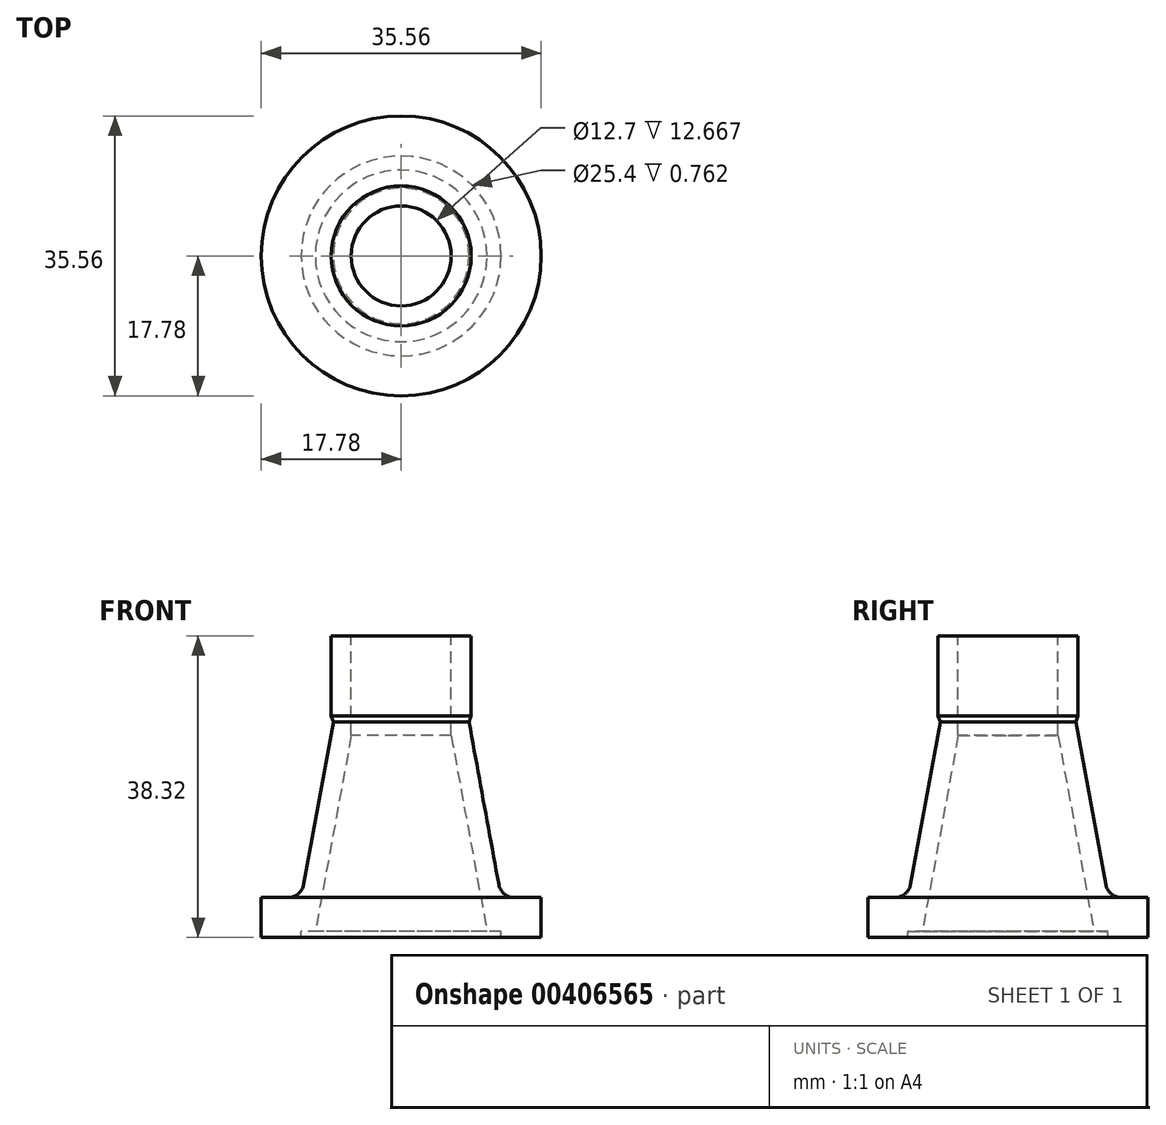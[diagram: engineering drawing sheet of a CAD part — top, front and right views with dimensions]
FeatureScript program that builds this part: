
annotation { "Feature Type Name" : "Feature", "Feature Type Description" : "" }
export const myFeature = defineFeature(function(context is Context, id is Id, definition is map)
    precondition{}
    {
        {
            var Q0;
            Q0=qCreatedBy(makeId("Front.planeOp"),FACE);
            var sketch = newSketch(context, id + "F0", { "sketchPlane" : qUnion([Q0])});
            skLineSegment(sketch, "E0", {"start": v(0, 25.5) * mm, "end": v(0, -29.47) * mm, "construction": true});
            skLineSegment(sketch, "E1", {"start": v(0, -17.71) * mm, "end": v(17.78, -17.71) * mm});
            skLineSegment(sketch, "E2", {"start": v(17.78, -17.71) * mm, "end": v(17.78, -12.63) * mm});
            skLineSegment(sketch, "E3", {"start": v(17.78, -12.63) * mm, "end": v(12.7, -12.63) * mm});
            skLineSegment(sketch, "E4", {"start": v(8.9, 10.45) * mm, "end": v(8.9, 20.61) * mm});
            skLineSegment(sketch, "E5", {"start": v(8.9, 20.61) * mm, "end": v(6.35, 20.61) * mm});
            skLineSegment(sketch, "E6", {"start": v(6.35, 20.61) * mm, "end": v(6.35, 7.94) * mm});
            skLineSegment(sketch, "E7", {"start": v(0, -16.95) * mm, "end": v(12.7, -16.95) * mm});
            skLineSegment(sketch, "E8", {"start": v(12.7, -16.95) * mm, "end": v(12.7, -17.71) * mm});
            skLineSegment(sketch, "E9", {"start": v(6.35, 20.61) * mm, "end": v(0, 20.61) * mm});
            skLineSegment(sketch, "E10", {"start": v(8.9, 10.45) * mm, "end": v(8.62, 9.67) * mm});
            skLineSegment(sketch, "E11", {"start": v(8.62, 9.67) * mm, "end": v(12.7, -12.63) * mm});
            skLineSegment(sketch, "E12", {"start": v(6.35, 7.94) * mm, "end": v(10.9, -16.95) * mm});
            skLineSegment(sketch, "E13", {"start": v(6.35, 7.94) * mm, "end": v(0, 7.94) * mm});
            skSolve(sketch);
        }
        {
            var Q0;
            {var subQ3=sQuery(id+"F0.wireOp",EDGE,"E2");Q0=makeQuery(id+"F0.imprint","IMPRINT",FACE,{"disambiguationData":[TD([[makeQuery(id+"F0.imprint","IMPRINT",EDGE,{"derivedFrom":subQ3}),1.0]])]});}
            var Q1;
            Q1=sQuery(id+"F0.wireOp",EDGE,"E0");
            revolve(context, id + "F1", {"entities" : qUnion([Q0]), "axis" : qUnion([Q1]), "revolveType" : RevolveType.FULL});
        }
        {
            var Q0;
            Q0=makeQuery(id+"F1.opRevolve","SWEPT_EDGE",EDGE,{"disambiguationData":[OSD([sQuery(id+"F0.wireOp",EDGE,"E3"),sQuery(id+"F0.wireOp",EDGE,"E11")])]});
            fillet(context, id + "F2", {"entities" : qUnion([Q0]), "radius" : 2.03 * mm, "tangentPropagation" : true, "allowEdgeOverflow" : false});
        }
    });
